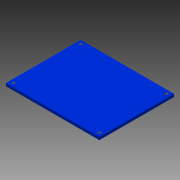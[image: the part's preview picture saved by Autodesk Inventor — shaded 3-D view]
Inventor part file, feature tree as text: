
AUTODESK INVENTOR PART (.ipt)
format: ipt  version: 2015 (Build 190159000, 159)  size: 96,256 bytes
history: native  units: mm
features: sketch x2, other x1, extrude x1, hole x1
ambient origin geometry x8: Origin, YZ Plane, XZ Plane, XY Plane, X Axis, Y Axis, Z Axis, Center Point
bodies: Body1 (feature_tree)
feature tree (5):
  other  "ソリッド1"
  extrude  "押し出し1"  Depth=100.0mm
  hole  "穴1"  [1 undecoded]
  sketch  "スケッチ1"
  sketch  "スケッチ2"
note: 1 required parameter value undecoded (feature->parameter linkage not recoverable at this tier; creation-order binding heuristic only, values carry confidence <= 0.55)
